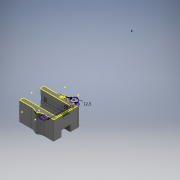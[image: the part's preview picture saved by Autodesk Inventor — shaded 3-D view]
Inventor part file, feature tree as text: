
AUTODESK INVENTOR PART (.ipt)
format: ipt  version: 2020 (Build 240168000, 168)  size: 350,208 bytes
history: native  units: mm
features: sketch x7, extrude x7, projected_geometry x3, fillet x2, hole x2, other x1, imported_body x1
ambient origin geometry x8: Origin, YZ Plane, XZ Plane, XY Plane, X Axis, Y Axis, Z Axis, Center Point
bodies: Body1 (feature_tree)
feature tree (23):
  other  "Твердое тело1"
  sketch  "Эскиз1"
  extrude  "Выдавливание1"  Depth=8.0mm
  fillet  "Сопряжение1"  Radius=12.5mm
  extrude  "Выдавливание2"  TaperAngle=0.0deg  [1 undecoded]
  extrude  "Выдавливание3"  Depth=2.5mm
  sketch  "Эскиз6"
  hole  "Отверстие1"  [1 undecoded]
  hole  "Отверстие2"  [1 undecoded]
  extrude  "Выдавливание4"  Depth=35.5mm
  sketch  "Эскиз7"
  sketch  "Эскиз8"
  extrude  "Выдавливание6"  Depth=25.0mm
  extrude  "Выдавливание5"  Depth=29.8mm
  fillet  "Сопряжение2"  Radius=9.933333mm
  extrude  "Выдавливание7"  Depth=5.0mm TaperAngle=0.0deg
  projected_geometry  "Спроецированная петля1"
  sketch  "Эскиз2"
  sketch  "Эскиз3"
  projected_geometry  "Спроецированная петля2"
  sketch  "Эскиз4"
  projected_geometry  "Спроецированная петля3"
  imported_body  "БазТело1"
note: 3 required parameter values undecoded (feature->parameter linkage not recoverable at this tier; creation-order binding heuristic only, values carry confidence <= 0.55)
